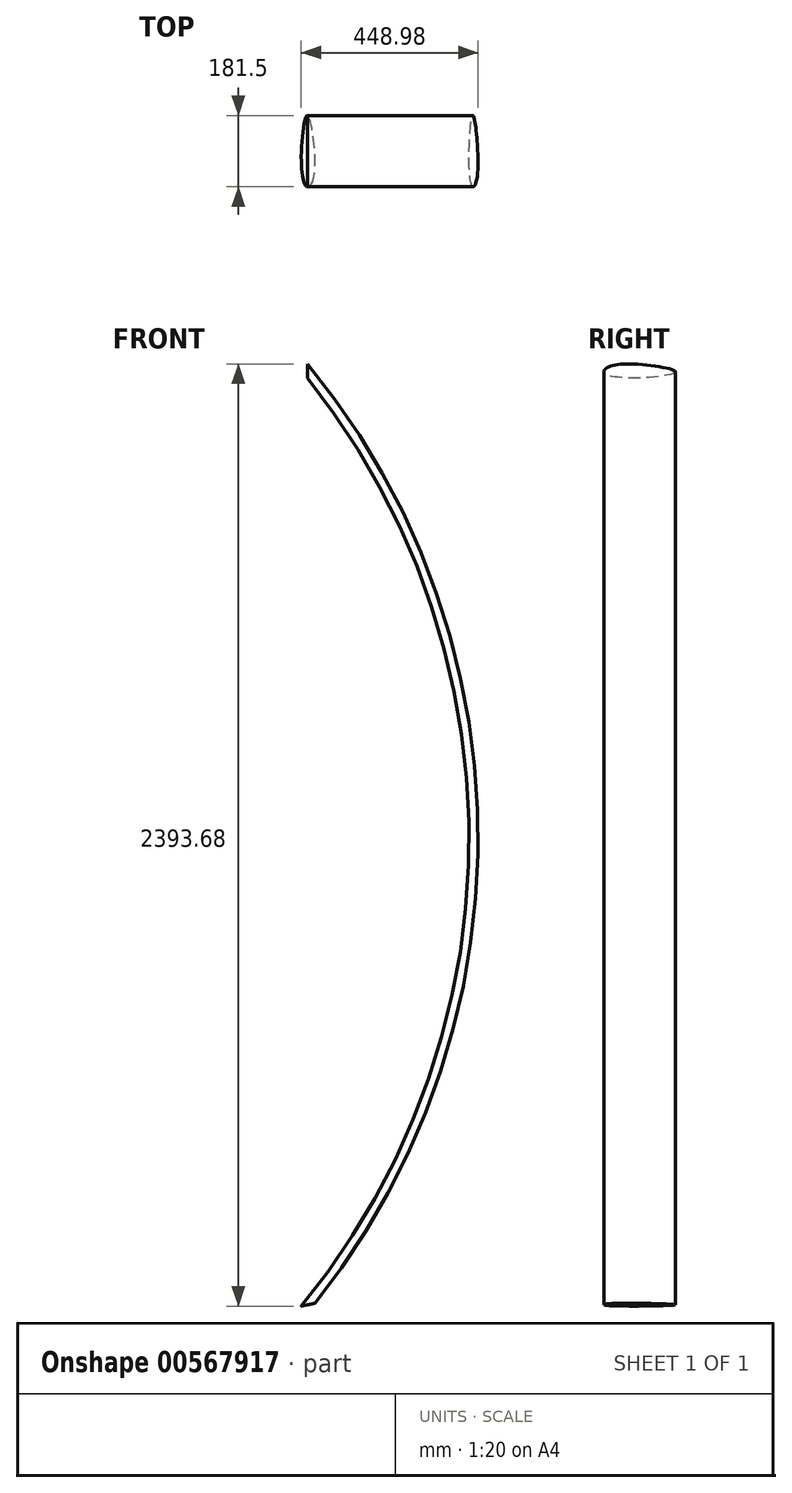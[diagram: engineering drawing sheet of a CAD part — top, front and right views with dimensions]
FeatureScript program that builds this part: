
annotation { "Feature Type Name" : "Feature", "Feature Type Description" : "" }
export const myFeature = defineFeature(function(context is Context, id is Id, definition is map)
    precondition{}
    {
        {
            var Q0;
            Q0=qCreatedBy(makeId("Right.planeOp"),FACE);
            var sketch = newSketch(context, id + "F0", { "sketchPlane" : qUnion([Q0])});
            skFitSpline(sketch, "E0", {"points": [v(0, 10.85) * mm, v(76.61, 19.6) * mm, v(173.65, 0) * mm, v(76.59, -15.6) * mm, v(0, -7.21) * mm, v(-7.82, 0) * mm, v(0, 10.85) * mm]});
            skSolve(sketch);
        }
        {
            var Q0;
            Q0=qCreatedBy(makeId("Front.planeOp"),FACE);
            var sketch = newSketch(context, id + "F1", { "sketchPlane" : qUnion([Q0])});
            skArc(sketch, "E1", {"start": v(0, -2370.16) * mm, "mid": v(420.74, -1185.08) * mm, "end": v(0, 0) * mm});
            skSolve(sketch);
        }
        {
            var Q0;
            Q0=makeQuery(id+"F0.imprint","IMPRINT",FACE,{"disambiguationData":[TD([[makeQuery(id+"F0.imprint","IMPRINT",EDGE,{"derivedFrom":sQuery(id+"F0.wireOp",EDGE,"E0")}),-1.0]])]});
            var Q1;
            Q1=sQuery(id+"F1.wireOp",EDGE,"E1");
            sweep(context, id + "F2", {"profiles" : qUnion([Q0]), "path" : qUnion([Q1])});
        }
    });
